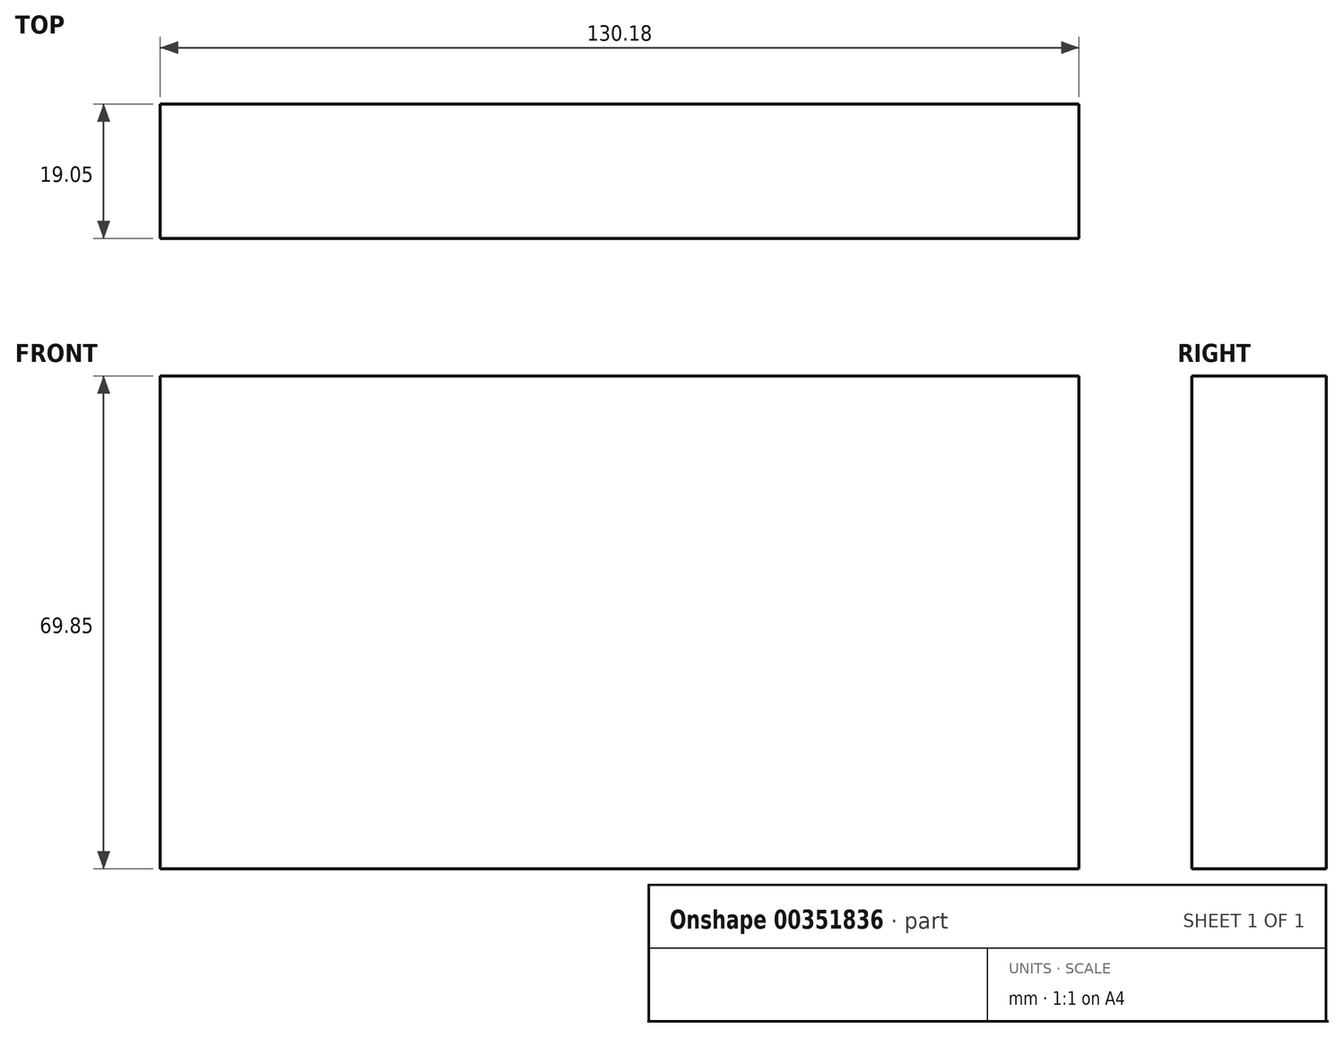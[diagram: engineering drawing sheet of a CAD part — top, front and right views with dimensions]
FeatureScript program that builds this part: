
annotation { "Feature Type Name" : "Feature", "Feature Type Description" : "" }
export const myFeature = defineFeature(function(context is Context, id is Id, definition is map)
    precondition{}
    {
        {
            var Q0;
            Q0=qCreatedBy(makeId("Front.planeOp"),FACE);
            var sketch = newSketch(context, id + "F0", { "sketchPlane" : qUnion([Q0])});
            skLineSegment(sketch, "E0.bottom", {"start": v(0, 0) * mm, "end": v(130.18, 0) * mm});
            skLineSegment(sketch, "E0.top", {"start": v(0, 69.85) * mm, "end": v(130.18, 69.85) * mm});
            skLineSegment(sketch, "E0.left", {"start": v(0, 0) * mm, "end": v(0, 69.85) * mm});
            skLineSegment(sketch, "E0.right", {"start": v(130.18, 0) * mm, "end": v(130.18, 69.85) * mm});
            skSolve(sketch);
        }
        {
            var Q0;
            Q0=makeQuery(id+"F0.imprint","IMPRINT",FACE,{"disambiguationData":[TD([[makeQuery(id+"F0.imprint","IMPRINT",EDGE,{"derivedFrom":sQuery(id+"F0.wireOp",EDGE,"E0.bottom")}),1.0]])]});
            extrude(context, id + "F1", {"entities" : qUnion([Q0]), "depth" : 19.05 * mm});
        }
    });
